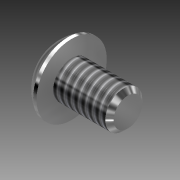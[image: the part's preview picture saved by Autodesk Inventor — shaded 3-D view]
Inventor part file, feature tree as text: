
AUTODESK INVENTOR PART (.ipt)
format: ipt  version: 2011 (Build 150239000, 239)  size: 120,320 bytes
history: native  units: in
note: dims shown in document units (in); Inventor stores cm internally (conversion verified against a paired STEP export)
features: other x1, imported_body x1, thread x1
ambient origin geometry x8: Origin, YZ Plane, XZ Plane, XY Plane, X Axis, Y Axis, Z Axis, Center Point
feature tree (3):
  parser-record x1  (decoder bookkeeping rows leaked as tree rows — omitted from the tree; the rows remain in map.json)
  imported_body  "Base1"
  thread  "Thread1"  [1 undecoded]
note: 1 required parameter value undecoded (feature->parameter linkage not recoverable at this tier; creation-order binding heuristic only, values carry confidence <= 0.55)
